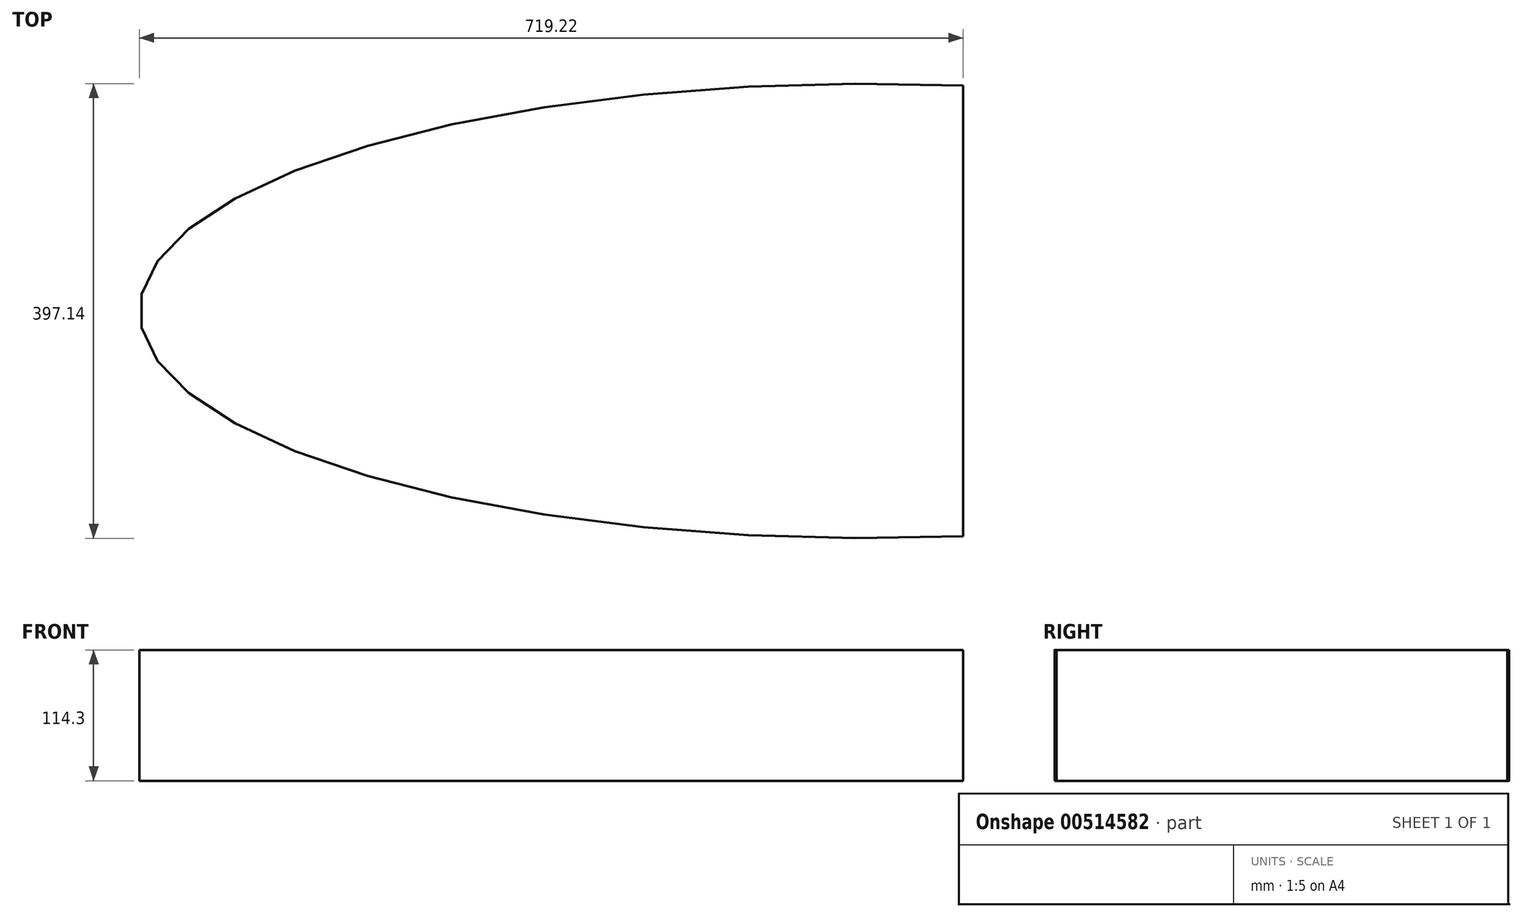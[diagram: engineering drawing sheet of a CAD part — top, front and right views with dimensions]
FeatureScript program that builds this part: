
annotation { "Feature Type Name" : "Feature", "Feature Type Description" : "" }
export const myFeature = defineFeature(function(context is Context, id is Id, definition is map)
    precondition{}
    {
        {
            var Q0;
            Q0=qCreatedBy(makeId("Top.planeOp"),FACE);
            var sketch = newSketch(context, id + "F0", { "sketchPlane" : qUnion([Q0])});
            skEllipse(sketch, "E0", {"center": v(-151.23, 24.28) * mm, "majorRadius": 637.13 * mm, "minorRadius": 198.57 * mm, "majorAxis": v(1, 0)});
            skLineSegment(sketch, "E1", {"start": v(-69.14, 221.2) * mm, "end": v(-69.14, -172.64) * mm});
            skSolve(sketch);
        }
        {
            var Q0;
            {var subQ0=sQuery(id+"F0.wireOp",EDGE,"E1");Q0=makeQuery(id+"F0.imprint","IMPRINT",FACE,{"disambiguationData":[TD([[makeQuery(id+"F0.imprint","IMPRINT",EDGE,{"derivedFrom":subQ0}),-1.0]])]});}
            extrude(context, id + "F1", {"entities" : qUnion([Q0]), "depth" : 114.3 * mm, "offsetDistance" : 25.4 * mm});
        }
    });
